# Revit family: Zumtobel CRAFT II Performance
name_source: partatom
category: Lighting Fixtures
revit_build: Autodesk Revit 2016 (Build: 20150220_1215(x64)
units: mm (PartAtom-declared; Revit-internal decimal feet)

## family parameters
Cut with Voids When Loaded = No
Host = Face
Light Source = Yes
OmniClass Number = 23.80.70.11
OmniClass Title = Luminaries for Internal Lighting
Part Type = Normal
Room Calculation Point = No
Round Connector Dimension = Use Diameter
Shared = No

## types (2) — shared parameters
Assembly Code = D5020200
Body = ZG_Metal_White
Color Filter = 16777215
Cover = ZG_Lamp_Self_llumination
Description = Pendant LED luminaire
Dimming Lamp Color Temperature Shift = <None>
Emit Shape Visible in Rendering = No
Emit from Rectangle Length = 414 mm  [stored 1.35827 ft]
Height = 77 mm
Lamp = LED
Manufacturer = Zumtobel Lighting
Tilt Angle = -90.00°
Voltage = 230 V
Width = 470 mm  [stored 1.54199 ft]
zero-valued in all types: Default Elevation

## per-type parameters (varying)
| type | Apparent Load | Craft L | Craft M | Emit from Rectangle Width | Length | Model | Photometric Web File | Suspension Distance | URL |
| CR2 M13k-840 PM WB LDO WH | 83 VA | No | Yes | 484 mm | 540 mm | 42187971 | 42187971_(STD_LEO).IES | 459 mm | www.zumtobel.com/42187971 |
| CR2 L35k-840 PC WB LDO WH | 224 VA | Yes | No | 989 mm  [stored 3.24475 ft] | 1045 mm | 42187604 | 42187604_(STD_LEO).IES | 964 mm | www.zumtobel.com/42187604 |

note: [stored X ft] marks values corroborated as IEEE doubles in the binary element streams (Revit-internal decimal feet)

## geometry (parser evidence)
native form markers: Sweep x7
no freeform markers — native parametric forms only
